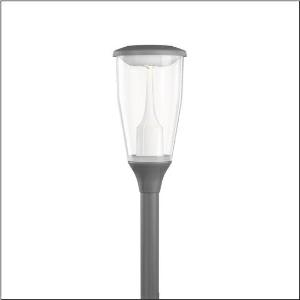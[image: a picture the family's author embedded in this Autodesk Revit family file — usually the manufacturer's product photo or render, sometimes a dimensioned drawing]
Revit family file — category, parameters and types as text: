
# Revit family: dl_11_iq___p1_0a_5xa5565lf14h000022_286d
name_source: partatom
category: Lighting Fixtures
units: mm (PartAtom-declared; Revit-internal decimal feet)

## family parameters
Cut with Voids When Loaded = No
Host = Face
Light Source = No
Part Type = Normal
Room Calculation Point = No
Round Connector Dimension = Use Diameter
Shared = No

## types (1)
- --- (1 x LED, 1530 lm, 10 W, 4000K)
    Apparent Load = 10 VA
    CIE Flux Codes = 34 63 91 95 100
    Color Rendering = 70
    Color Temperature = 4000K
    Default Elevation = 1800 mm
    Description = DL 11 iQ, mast luminaire, Module 540 iQ-SR, primary light control with 3 zone facetted reflector, of plastic, silver coated, highly specular, structured, primary optical cover: cover, of PMMA, transparent, light distribution: P1.0a, light emission: direct distribution, primary light characteristic: asymmetric, installation type: post-top, LED, High Power LED, rated luminous flux: 1.560lm, luminous efficacy: 149lm/W, light colour: 740, colour temperature: 4000K, control: Street-Remote, Auto-Match, Temp-Guard, Lumen-Switch, Night-Set, Smart-Wire, Light-Fading, Desk-Remote (wireless, voltage-free reading and setting of iQ features in the workshop via application-optimized NFC function/RFID function), optimised constant luminous flux control (CLO 2.0), mains connection: 220..240V, AC, 50/60Hz, connection cable pre-assembled, cable length: 5,5m, start of lifetime: 10W, end of service life: 10W, reduction: 5W, luminaire housing, upper part, of diecast aluminium, coated, Siteco® metallic grey (DB 702S), spigot size: 60mm (post-top), post-top mast mounting element, of diecast aluminium, coated, Siteco® metallic grey (DB 702S), Module 540 iQ-SR, traffic white (RAL 9016), equipment: standard, protection rating (complete): IP66, insulation class (complete): insulation class II (safety insulation), certification: CE, ENEC, ENEC+, VDE, packaging unit: 1 piece

Light Distribution: P1.0a
    Height = 665 mm
    Lamp = 1 x LED
    Lamp Light Flux = 1530 lm
    Lamp Power = 10 W
    Lamp count = 1
    Length = 334 mm
    Luminous efficacy = 153 lm/W
    Manufacturer = Siteco
    ModVariant = No
    Model = 5XA5565LF14H000022
    Number of Poles = 1
    OnlyDefault = Yes
    Power Factor = 1
    Product Name = DL 11 iQ | P1.0a
    Product group = mast luminaire | pylon top
    ProductGroupID = 6100
    Protection Class = Protection class II
    Protection Degree = IP 66
    RLX_Detail_Level = 1
    RLX_Emergency_Light_Flux = 0 lm
    RLX_Emergency_Type = 0
    RLX_Emergency_Type_DB = No
    RlxData = <blob elided: 108681 chars, md5=afa8e1ca>
    Socket = socket
    Standby Power = 0 W
    System Light Flux = 1530 lm
    System Power = 10 W
    Type Comments = factory setting: luminous flux: 100 % | dim-lin: 254 | 401 mA
    Type Image = l_1258354.jpg
    URL = http://relux.com
    VarID = @adj_024247
    Voltage = 0 V
    Weight = 0.00 kg
    Width = 0 mm  [stored 0 ft]

note: [stored X ft] marks values corroborated as IEEE doubles in the binary element streams (Revit-internal decimal feet)

## geometry (parser evidence)
native form markers: Blend x4, Sweep x10
no freeform markers — native parametric forms only
